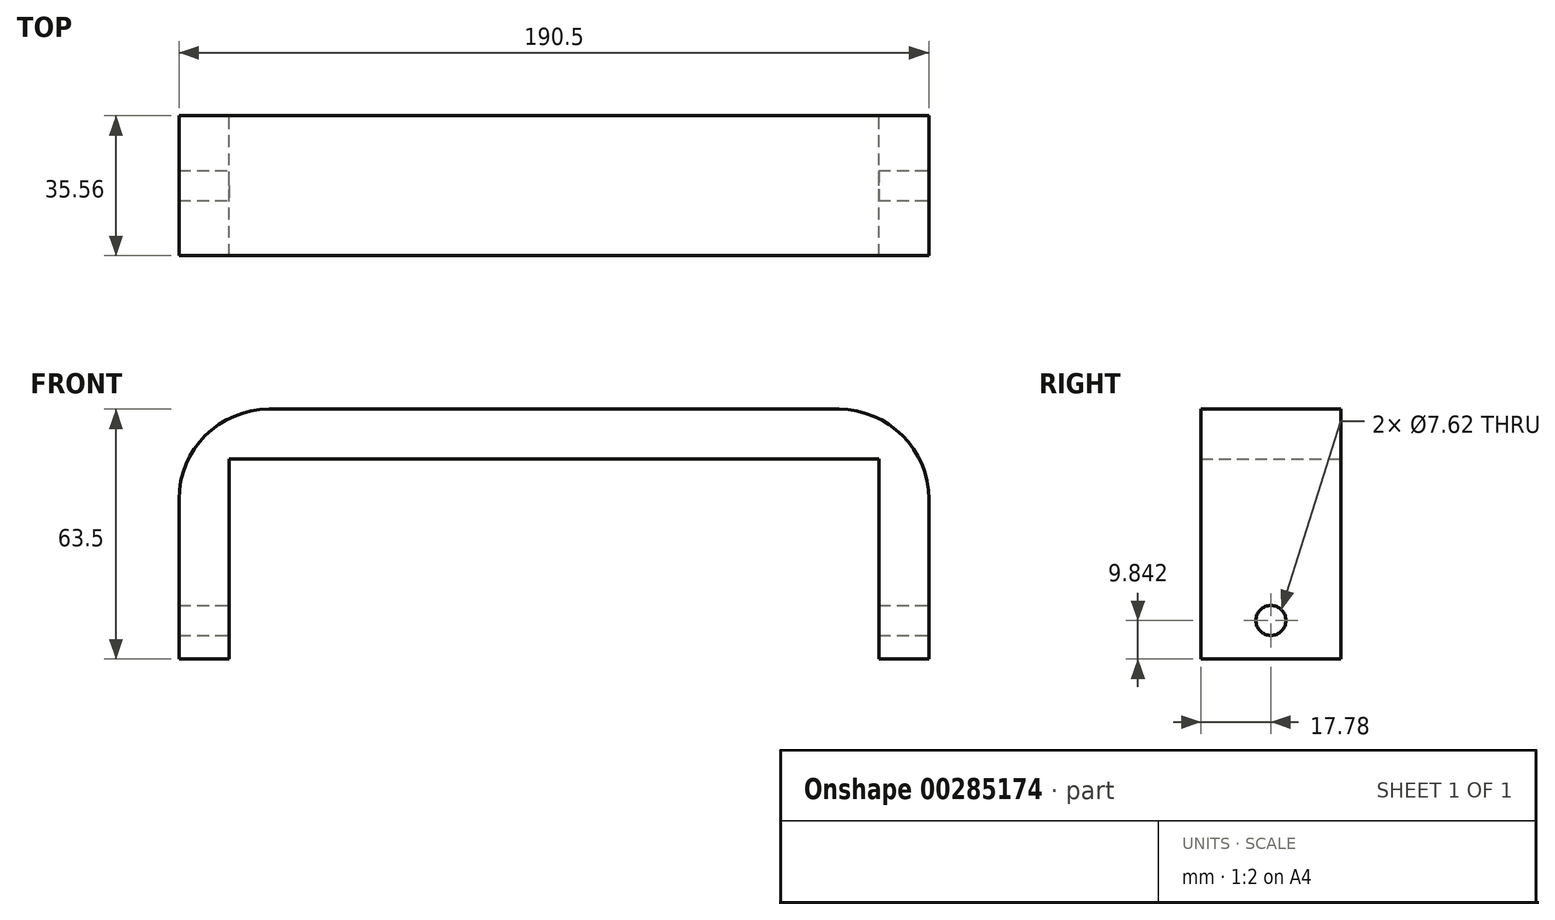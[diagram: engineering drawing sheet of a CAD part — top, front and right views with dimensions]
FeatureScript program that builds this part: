
annotation { "Feature Type Name" : "Feature", "Feature Type Description" : "" }
export const myFeature = defineFeature(function(context is Context, id is Id, definition is map)
    precondition{}
    {
        {
            var Q0;
            Q0=qCreatedBy(makeId("Front.planeOp"),FACE);
            var sketch = newSketch(context, id + "F0", { "sketchPlane" : qUnion([Q0])});
            skLineSegment(sketch, "E0", {"start": v(0, 0) * mm, "end": v(12.7, 0) * mm});
            skLineSegment(sketch, "E1", {"start": v(12.7, 0) * mm, "end": v(12.7, 50.8) * mm});
            skLineSegment(sketch, "E2", {"start": v(12.7, 50.8) * mm, "end": v(177.8, 50.8) * mm});
            skLineSegment(sketch, "E3", {"start": v(177.8, 50.8) * mm, "end": v(177.8, 0) * mm});
            skLineSegment(sketch, "E4", {"start": v(177.8, 0) * mm, "end": v(190.5, 0) * mm});
            skLineSegment(sketch, "E5", {"start": v(190.5, 0) * mm, "end": v(190.5, 63.5) * mm});
            skLineSegment(sketch, "E6", {"start": v(190.5, 63.5) * mm, "end": v(0, 63.5) * mm});
            skLineSegment(sketch, "E7", {"start": v(0, 63.5) * mm, "end": v(0, 0) * mm});
            skSolve(sketch);
        }
        {
            var Q0;
            Q0=makeQuery(id+"F0.imprint","IMPRINT",FACE,{"disambiguationData":[TD([[makeQuery(id+"F0.imprint","IMPRINT",EDGE,{"derivedFrom":sQuery(id+"F0.wireOp",EDGE,"E0")}),1.0]])]});
            extrude(context, id + "F1", {"entities" : qUnion([Q0]), "depth" : 35.56 * mm});
        }
        {
            var Q0;
            Q0=makeQuery(id+"F1.opExtrude","SWEPT_EDGE",EDGE,{"disambiguationData":[OSD([sQuery(id+"F0.wireOp",EDGE,"E6"),sQuery(id+"F0.wireOp",EDGE,"E7")])]});
            var Q1;
            Q1=makeQuery(id+"F1.opExtrude","SWEPT_EDGE",EDGE,{"disambiguationData":[OSD([sQuery(id+"F0.wireOp",EDGE,"E5"),sQuery(id+"F0.wireOp",EDGE,"E6")])]});
            fillet(context, id + "F2", {"entities" : qUnion([Q0, Q1]), "radius" : 22.86 * mm, "tangentPropagation" : true, "allowEdgeOverflow" : false});
        }
        {
            var Q0;
            Q0=makeQuery(id+"F1.opExtrude","SWEPT_FACE",FACE,{"disambiguationData":[OSD([sQuery(id+"F0.wireOp",EDGE,"E5")])]});
            var sketch = newSketch(context, id + "F3", { "sketchPlane" : qUnion([Q0])});
            skLineSegment(sketch, "E8", {"start": v(-17.78, 40.64) * mm, "end": v(-17.78, 0) * mm, "construction": true});
            skLineSegment(sketch, "E9.bottom", {"start": v(-35.56, 40.64) * mm, "end": v(0, 40.64) * mm, "construction": true});
            skLineSegment(sketch, "E9.top", {"start": v(-35.56, 0) * mm, "end": v(0, 0) * mm, "construction": true});
            skLineSegment(sketch, "E9.left", {"start": v(-35.56, 40.64) * mm, "end": v(-35.56, 0) * mm, "construction": true});
            skLineSegment(sketch, "E9.right", {"start": v(0, 40.64) * mm, "end": v(0, 0) * mm, "construction": true});
            skCircle(sketch, "E10", {"center": v(-17.78, 9.84) * mm, "radius": 3.81 * mm});
            skSolve(sketch);
        }
        {
            var Q0;
            Q0=makeQuery(id+"F3.imprint","IMPRINT",FACE,{"disambiguationData":[TD([[makeQuery(id+"F3.imprint","IMPRINT",EDGE,{"derivedFrom":sQuery(id+"F3.wireOp",EDGE,"E10")}),1.0]])]});
            extrude(context, id + "F4", {"entities" : qUnion([Q0]), "operationType" : NewBodyOperationType.REMOVE, "endBound" : BoundingType.THROUGH_ALL, "oppositeDirection" : true, "depth" : 25.4 * mm});
        }
    });
